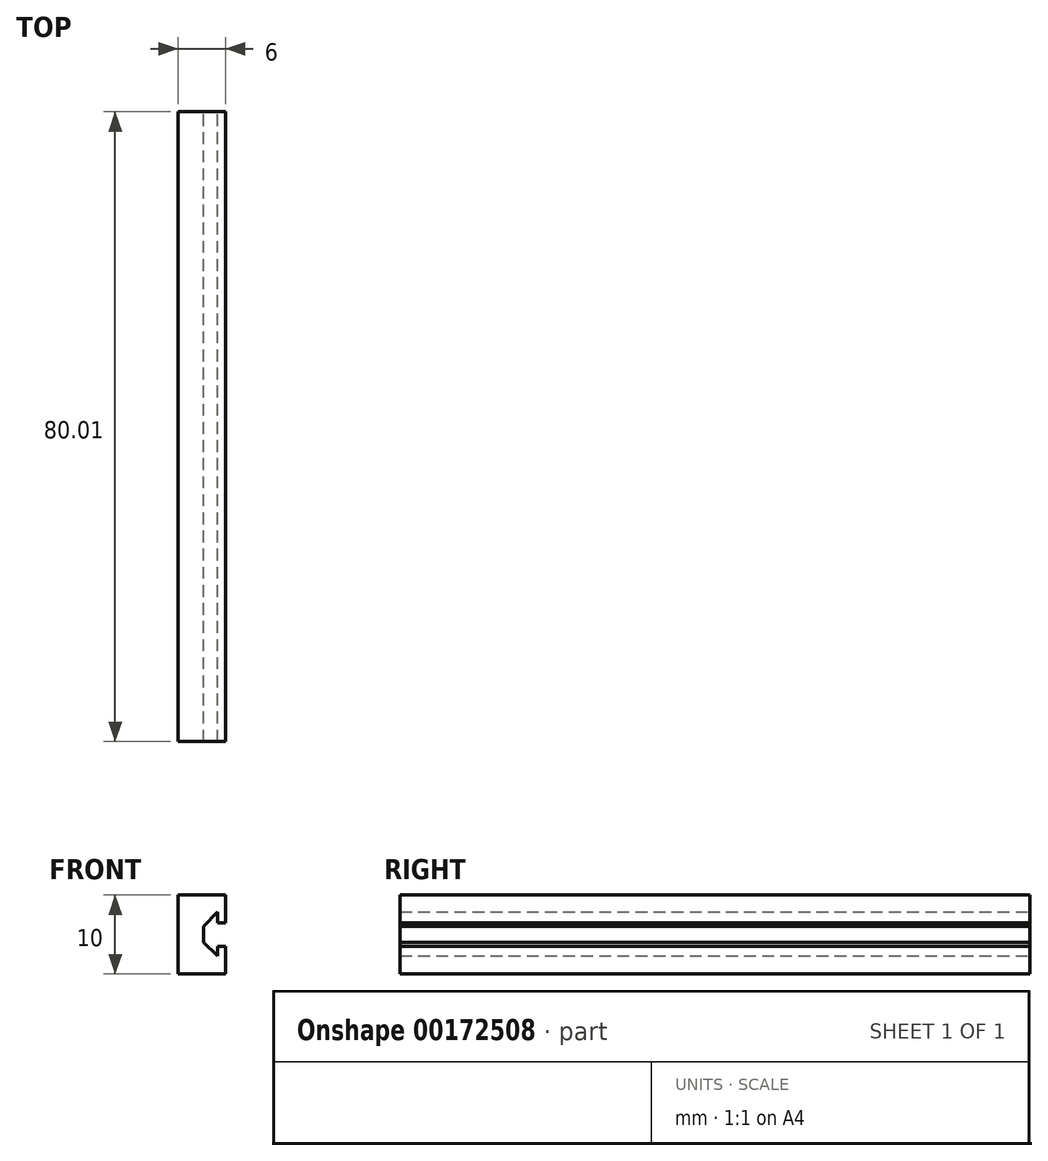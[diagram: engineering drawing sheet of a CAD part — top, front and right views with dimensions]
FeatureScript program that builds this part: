
annotation { "Feature Type Name" : "Feature", "Feature Type Description" : "" }
export const myFeature = defineFeature(function(context is Context, id is Id, definition is map)
    precondition{}
    {
        {
            var Q0;
            Q0=qCreatedBy(makeId("Front.planeOp"),FACE);
            var sketch = newSketch(context, id + "F0", { "sketchPlane" : qUnion([Q0])});
            skLineSegment(sketch, "E0.0.0", {"start": v(-3.25, -23.67) * mm, "end": v(2.75, -23.67) * mm});
            skLineSegment(sketch, "E0.0.1", {"start": v(2.75, -23.67) * mm, "end": v(2.75, -20.17) * mm});
            skLineSegment(sketch, "E0.0.2", {"start": v(2.75, -20.17) * mm, "end": v(1.75, -20.17) * mm});
            skLineSegment(sketch, "E0.0.3", {"start": v(1.75, -20.17) * mm, "end": v(1.75, -21.4) * mm});
            skLineSegment(sketch, "E0.0.4", {"start": v(1.75, -21.4) * mm, "end": v(-0.05, -19.67) * mm});
            skLineSegment(sketch, "E0.0.5", {"start": v(-0.05, -19.67) * mm, "end": v(-0.05, -17.67) * mm});
            skLineSegment(sketch, "E0.0.6", {"start": v(-0.05, -17.67) * mm, "end": v(1.75, -15.8) * mm});
            skLineSegment(sketch, "E0.0.7", {"start": v(1.75, -15.8) * mm, "end": v(1.75, -17.17) * mm});
            skLineSegment(sketch, "E0.0.8", {"start": v(1.75, -17.17) * mm, "end": v(2.75, -17.17) * mm});
            skLineSegment(sketch, "E0.0.9", {"start": v(2.75, -17.17) * mm, "end": v(2.75, -13.67) * mm});
            skLineSegment(sketch, "E0.0.10", {"start": v(2.75, -13.67) * mm, "end": v(-3.25, -13.67) * mm});
            skLineSegment(sketch, "E0.0.11", {"start": v(-3.25, -13.67) * mm, "end": v(-3.25, -23.67) * mm});
            skSolve(sketch);
        }
        {
            var Q0;
            Q0=makeQuery(id+"F0.imprint","IMPRINT",FACE,{"disambiguationData":[TD([[makeQuery(id+"F0.imprint","IMPRINT",EDGE,{"derivedFrom":sQuery(id+"F0.wireOp",EDGE,"E0.0.0")}),1.0]])]});
            extrude(context, id + "F1", {"entities" : qUnion([Q0]), "depth" : 80 * mm});
        }
    });
